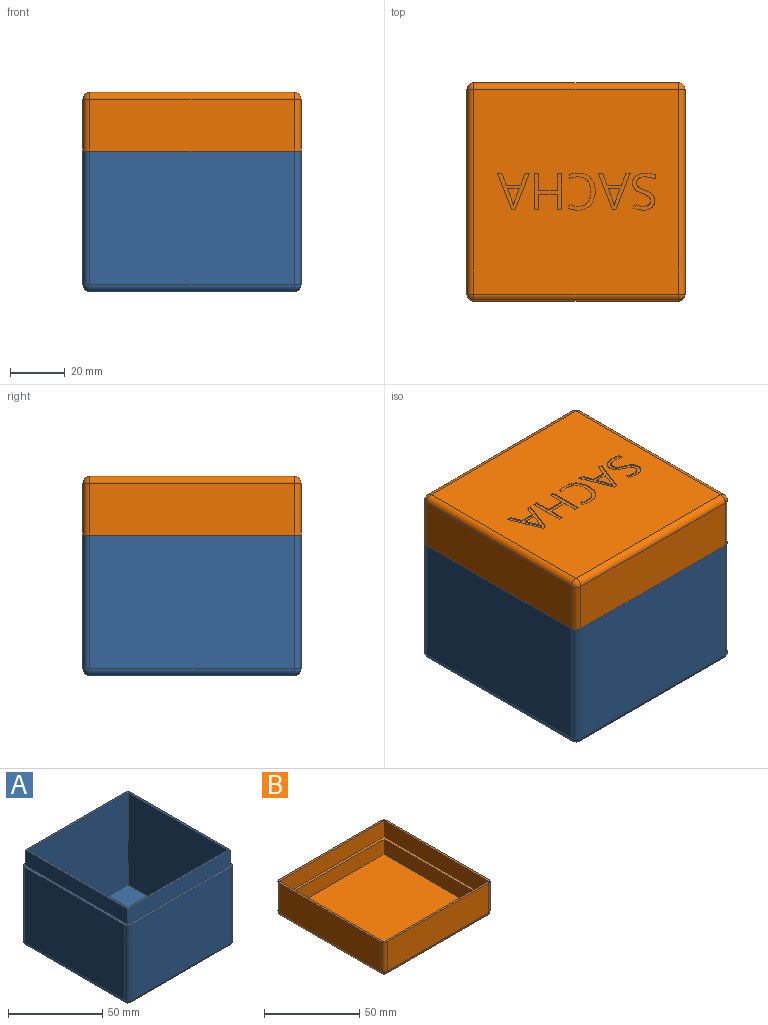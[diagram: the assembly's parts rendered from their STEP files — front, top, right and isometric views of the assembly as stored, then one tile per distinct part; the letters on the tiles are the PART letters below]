
ASSEMBLY  parts=2 mates=1
PART A: 28 faces, bbox 80x80x61.5 mm
  f0: plane 80x80mm, normal (0,0,1), area 496.4mm2, adj f1,f2,f3,f4,f6,f8,f11,f17
  f1: plane 75x49mm, normal (1,0,0), area 3675mm2, adj f0,f11,f15,f17
  f2: plane 75x49mm, normal (0,1,0), area 3675mm2, adj f0,f8,f14,f17
  f3: plane 75x49mm, normal (-1,0,0), area 3675mm2, adj f0,f6,f8,f9
  f4: plane 75x49mm, normal (0,-1,0), area 3675mm2, adj f0,f6,f10,f11
  f5: plane 75x75mm, normal (0,0,-1), area 5625mm2, adj f9,f10,f14,f15
  f6: cylinder r=2.5mm len=49mm, axis (0,0,1), area 192.4mm2, adj f0,f3,f4,f7
  f7: sphere r=2.5mm, area 9.8mm2, adj f6,f9,f10
  f8: cylinder r=2.5mm len=49mm, axis (0,0,-1), area 192.4mm2, adj f0,f2,f3,f12
  f9: cylinder r=2.5mm len=75mm, axis (0,-1,0), area 294.5mm2, adj f3,f5,f7,f12
  f10: cylinder r=2.5mm len=75mm, axis (1,0,0), area 294.5mm2, adj f4,f5,f7,f13
  f11: cylinder r=2.5mm len=49mm, axis (0,0,-1), area 192.4mm2, adj f0,f1,f4,f13
  f12: sphere r=2.5mm, area 9.8mm2, adj f8,f9,f14
  f13: sphere r=2.5mm, area 9.8mm2, adj f10,f11,f15
  f14: cylinder r=2.5mm len=75mm, axis (-1,0,0), area 294.5mm2, adj f2,f5,f12,f16
  f15: cylinder r=2.5mm len=75mm, axis (0,1,0), area 294.5mm2, adj f1,f5,f13,f16
  f16: sphere r=2.5mm, area 9.8mm2, adj f14,f15,f17
  f17: cylinder r=2.5mm len=49mm, axis (0,0,1), area 192.4mm2, adj f0,f1,f2,f16
  f18: plane 76.8x10mm, normal (0,-1,0), area 768mm2, adj f0,f19,f21,f22
  f19: plane 76.8x10mm, normal (1,0,0), area 768mm2, adj f0,f18,f20,f22
  f20: plane 76.8x10mm, normal (0,1,0), area 768mm2, adj f0,f19,f21,f22
  f21: plane 76.8x10mm, normal (-1,0,0), area 768mm2, adj f0,f18,f20,f22
  f22: plane 76.8x76.8mm, normal (0,0,1), area 362.9mm2, adj f18,f19,f20,f21,f24,f25,f26,f27
  f23: plane 74.4x74.4mm, normal (0,0,1), area 5535.4mm2, adj f24,f25,f26,f27
  f24: plane 74.4x60mm, normal (0,-1,0), area 4464mm2, adj f22,f23,f25,f27
  f25: plane 74.4x60mm, normal (1,0,0), area 4464mm2, adj f22,f23,f24,f26
  f26: plane 74.4x60mm, normal (0,1,0), area 4464mm2, adj f22,f23,f25,f27
  f27: plane 74.4x60mm, normal (-1,0,0), area 4464mm2, adj f22,f23,f24,f26
PART B: 113 faces, bbox 80x80x21.5 mm
  f0: plane 75x75mm, normal (0,0,-1), area 5382.9mm2, adj f19,f20,f24,f25,f28,f29,f30,f31
  f1: plane 75x19mm, normal (1,0,0), area 1425mm2, adj f5,f21,f25,f27
  f2: plane 75x19mm, normal (0,1,0), area 1425mm2, adj f5,f18,f24,f27
  f3: plane 75x19mm, normal (-1,0,0), area 1425mm2, adj f5,f16,f18,f19
  f4: plane 75x19mm, normal (0,-1,0), area 1425mm2, adj f5,f16,f20,f21
  f5: plane 80x80mm, normal (0,0,1), area 372.9mm2, adj f1,f2,f3,f4,f6,f7,f8,f9
  f6: plane 77.6x10.4mm, normal (0,-1,0), area 807mm2, adj f5,f7,f9,f10
  f7: plane 77.6x10.4mm, normal (1,0,0), area 807mm2, adj f5,f6,f8,f10
  f8: plane 77.6x10.4mm, normal (0,1,0), area 807mm2, adj f5,f7,f9,f10
  f9: plane 77.6x10.4mm, normal (-1,0,0), area 807mm2, adj f5,f6,f8,f10
  f10: plane 77.6x77.6mm, normal (0,0,1), area 486.4mm2, adj f6,f7,f8,f9,f12,f13,f14,f15
  f11: plane 74.4x74.4mm, normal (0,0,1), area 5535.4mm2, adj f12,f13,f14,f15
  f12: plane 74.4x9.6mm, normal (0,1,0), area 714.2mm2, adj f10,f11,f13,f15
  f13: plane 74.4x9.6mm, normal (-1,0,0), area 714.2mm2, adj f10,f11,f12,f14
  f14: plane 74.4x9.6mm, normal (0,-1,0), area 714.2mm2, adj f10,f11,f13,f15
  f15: plane 74.4x9.6mm, normal (1,0,0), area 714.2mm2, adj f10,f11,f12,f14
  f16: cylinder r=2.5mm len=19mm, axis (0,0,1), area 74.6mm2, adj f3,f4,f5,f17
  f17: sphere r=2.5mm, area 9.8mm2, adj f16,f19,f20
  f18: cylinder r=2.5mm len=19mm, axis (0,0,-1), area 74.6mm2, adj f2,f3,f5,f22
  f19: cylinder r=2.5mm len=75mm, axis (0,-1,0), area 294.5mm2, adj f0,f3,f17,f22
  f20: cylinder r=2.5mm len=75mm, axis (1,0,0), area 294.5mm2, adj f0,f4,f17,f23
  f21: cylinder r=2.5mm len=19mm, axis (0,0,-1), area 74.6mm2, adj f1,f4,f5,f23
  f22: sphere r=2.5mm, area 9.8mm2, adj f18,f19,f24
  f23: sphere r=2.5mm, area 9.8mm2, adj f20,f21,f25
  f24: cylinder r=2.5mm len=75mm, axis (-1,0,0), area 294.5mm2, adj f0,f2,f22,f26
  f25: cylinder r=2.5mm len=75mm, axis (0,1,0), area 294.5mm2, adj f0,f1,f23,f26
  f26: sphere r=2.5mm, area 9.8mm2, adj f24,f25,f27
  f27: cylinder r=2.5mm len=19mm, axis (0,0,1), area 74.6mm2, adj f1,f2,f5,f26
  f28: extruded ~3.43x1.45mm, area 1.5mm2, adj f0,f29,f42,f43
  f29: extruded ~3x0.7mm, area 1.2mm2, adj f0,f28,f30,f43
  f30: plane 1.32x0.65mm, normal (-0.9,-0.44,0), area 0.6mm2, adj f0,f29,f31,f43
  f31: extruded ~3.63x0.76mm, area 1.5mm2, adj f0,f30,f32,f43
  f32: extruded ~3.39x0.83mm, area 1.4mm2, adj f0,f31,f33,f43
  f33: extruded ~2.36x2.2mm, area 1.3mm2, adj f0,f32,f34,f43
  f34: extruded ~3.57x0.76mm, area 1.5mm2, adj f0,f33,f35,f43
  f35: extruded ~5.03x1.58mm, area 2.2mm2, adj f0,f34,f36,f43
  f36: extruded ~4.5x1.77mm, area 2mm2, adj f0,f35,f37,f43
  f37: extruded ~3.38x0.52mm, area 1.4mm2, adj f0,f36,f38,f43
  f38: plane 1.34x0.4mm, normal (-1,0,0), area 0.5mm2, adj f0,f37,f39,f43
  f39: extruded ~3.15x0.5mm, area 1.3mm2, adj f0,f38,f40,f43
  f40: extruded ~3.46x1.41mm, area 1.5mm2, adj f0,f39,f41,f43
  f41: extruded ~4x1.21mm, area 1.7mm2, adj f0,f40,f42,f43
  f42: extruded ~3.96x1.26mm, area 1.7mm2, adj f0,f28,f41,f43
  f43: plane 13.56x9.98mm, normal (0,0,-1), area 38mm2, adj f28,f29,f30,f31,f32,f33,f34,f35
  f44: plane 1.53x0.4mm, normal (0,-1,0), area 0.6mm2, adj f0,f45,f55,f56
  f45: plane 13.19x0.4mm, normal (-1,0,0), area 5.3mm2, adj f0,f44,f46,f56
  f46: plane 1.53x0.4mm, normal (0,1,0), area 0.6mm2, adj f0,f45,f47,f56
  f47: plane 5.61x0.4mm, normal (1,0,0), area 2.2mm2, adj f0,f46,f48,f56
  f48: plane 6.95x0.4mm, normal (0,1,0), area 2.8mm2, adj f0,f47,f49,f56
  f49: plane 5.61x0.4mm, normal (-1,0,0), area 2.2mm2, adj f0,f48,f50,f56
  f50: plane 1.53x0.4mm, normal (0,1,0), area 0.6mm2, adj f0,f49,f51,f56
  f51: plane 13.19x0.4mm, normal (1,0,0), area 5.3mm2, adj f0,f50,f52,f56
  f52: plane 1.53x0.4mm, normal (0,-1,0), area 0.6mm2, adj f0,f51,f53,f56
  f53: plane 6.21x0.4mm, normal (-1,0,0), area 2.5mm2, adj f0,f52,f54,f56
  f54: plane 6.95x0.4mm, normal (0,-1,0), area 2.8mm2, adj f0,f53,f55,f56
  f55: plane 6.21x0.4mm, normal (1,0,0), area 2.5mm2, adj f0,f44,f54,f56
  f56: plane 13.19x10.01mm, normal (0,0,-1), area 49.9mm2, adj f44,f45,f46,f47,f48,f49,f50,f51
  f57: plane 4.09x1.54mm, normal (0.94,-0.35,0), area 1.7mm2, adj f58,f69,f70,f111
  f58: plane 4.27x0.4mm, normal (0,1,0), area 1.7mm2, adj f57,f59,f70,f111
  f59: plane 4.09x1.55mm, normal (-0.94,-0.35,0), area 1.7mm2, adj f58,f60,f70,f111
  f60: extruded ~1.9x0.57mm, area 0.8mm2, adj f59,f69,f70,f111
  f61: plane 4.19x1.64mm, normal (0.93,-0.36,0), area 1.8mm2, adj f0,f62,f68,f70
  f62: plane 1.59x0.4mm, normal (0,-1,0), area 0.6mm2, adj f0,f61,f63,f70
  f63: plane 13.24x5.19mm, normal (-0.93,0.36,0), area 5.7mm2, adj f0,f62,f64,f70
  f64: plane 1.29x0.4mm, normal (0,1,0), area 0.5mm2, adj f0,f63,f65,f70
  f65: plane 13.24x5.21mm, normal (0.93,0.37,0), area 5.7mm2, adj f0,f64,f66,f70
  f66: plane 1.55x0.4mm, normal (0,-1,0), area 0.6mm2, adj f0,f65,f67,f70
  f67: plane 4.19x1.62mm, normal (-0.93,-0.36,0), area 1.8mm2, adj f0,f66,f68,f70
  f68: plane 5.28x0.4mm, normal (0,-1,0), area 2.1mm2, adj f0,f61,f67,f70
  f69: extruded ~1.9x0.61mm, area 0.8mm2, adj f57,f60,f70,f111
  f70: plane 13.24x11.69mm, normal (0,0,-1), area 44.7mm2, adj f57,f58,f59,f60,f61,f62,f63,f64
  f71: plane 4.09x1.54mm, normal (0.94,-0.35,0), area 1.7mm2, adj f72,f83,f84,f112
  f72: plane 4.27x0.4mm, normal (0,1,0), area 1.7mm2, adj f71,f73,f84,f112
  f73: plane 4.09x1.55mm, normal (-0.94,-0.35,0), area 1.7mm2, adj f72,f74,f84,f112
  f74: extruded ~1.9x0.57mm, area 0.8mm2, adj f73,f83,f84,f112
  f75: plane 4.19x1.64mm, normal (0.93,-0.36,0), area 1.8mm2, adj f0,f76,f82,f84
  f76: plane 1.59x0.4mm, normal (0,-1,0), area 0.6mm2, adj f0,f75,f77,f84
  f77: plane 13.24x5.19mm, normal (-0.93,0.36,0), area 5.7mm2, adj f0,f76,f78,f84
  f78: plane 1.29x0.4mm, normal (0,1,0), area 0.5mm2, adj f0,f77,f79,f84
  f79: plane 13.24x5.21mm, normal (0.93,0.37,0), area 5.7mm2, adj f0,f78,f80,f84
  f80: plane 1.55x0.4mm, normal (0,-1,0), area 0.6mm2, adj f0,f79,f81,f84
  f81: plane 4.19x1.62mm, normal (-0.93,-0.36,0), area 1.8mm2, adj f0,f80,f82,f84
  f82: plane 5.28x0.4mm, normal (0,-1,0), area 2.1mm2, adj f0,f75,f81,f84
  f83: extruded ~1.9x0.61mm, area 0.8mm2, adj f71,f74,f84,f112
  f84: plane 13.24x11.69mm, normal (0,0,-1), area 44.7mm2, adj f71,f72,f73,f74,f75,f76,f77,f78
  f85: extruded ~2.72x1.26mm, area 1.2mm2, adj f0,f86,f109,f110
  f86: extruded ~2.2x0.78mm, area 1mm2, adj f0,f85,f87,f110
  f87: extruded ~2.85x1.59mm, area 1.3mm2, adj f0,f86,f88,f110
  f88: extruded ~1.84x0.81mm, area 0.8mm2, adj f0,f87,f89,f110
  f89: extruded ~0.85x0.8mm, area 0.5mm2, adj f0,f88,f90,f110
  f90: extruded ~1.12x0.4mm, area 0.5mm2, adj f0,f89,f91,f110
  f91: extruded ~1.45x0.69mm, area 0.7mm2, adj f0,f90,f92,f110
  f92: extruded ~1.9x0.52mm, area 0.8mm2, adj f0,f91,f93,f110
  f93: extruded ~3.18x0.68mm, area 1.3mm2, adj f0,f92,f94,f110
  f94: plane 1.33x0.48mm, normal (-0.94,-0.34,0), area 0.6mm2, adj f0,f93,f95,f110
  f95: extruded ~3.62x0.72mm, area 1.5mm2, adj f0,f94,f96,f110
  f96: extruded ~3.03x0.9mm, area 1.3mm2, adj f0,f95,f97,f110
  f97: extruded ~2.43x1.14mm, area 1.1mm2, adj f0,f96,f98,f110
  f98: extruded ~2.35x0.79mm, area 1mm2, adj f0,f97,f99,f110
  f99: extruded ~2.63x1.56mm, area 1.2mm2, adj f0,f98,f100,f110
  f100: extruded ~1.96x0.84mm, area 0.9mm2, adj f0,f99,f101,f110
  f101: extruded ~0.92x0.81mm, area 0.5mm2, adj f0,f100,f102,f110
  f102: extruded ~1.12x0.4mm, area 0.5mm2, adj f0,f101,f103,f110
  f103: extruded ~1.62x0.78mm, area 0.7mm2, adj f0,f102,f104,f110
  f104: extruded ~2.31x0.58mm, area 1mm2, adj f0,f103,f105,f110
  f105: extruded ~1.89x0.4mm, area 0.8mm2, adj f0,f104,f106,f110
  f106: extruded ~1.77x0.54mm, area 0.7mm2, adj f0,f105,f107,f110
  f107: plane 1.48x0.4mm, normal (1,0,0), area 0.6mm2, adj f0,f106,f108,f110
  f108: extruded ~3.61x0.61mm, area 1.5mm2, adj f0,f107,f109,f110
  f109: extruded ~3.43x0.98mm, area 1.5mm2, adj f0,f85,f108,f110
  f110: plane 13.56x8.3mm, normal (0,0,-1), area 40.3mm2, adj f85,f86,f87,f88,f89,f90,f91,f92
  f111: plane 5.99x4.27mm, normal (0,0,-1), area 12.2mm2, adj f57,f58,f59,f60,f69
  f112: plane 5.99x4.27mm, normal (0,0,-1), area 12.2mm2, adj f71,f72,f73,f74,f83
PLACE A t=(-21.85,-4.63,-18.77)mm fixed
PLACE B rot(axis=(0,1,0),180deg) t=(-21.85,-4.63,54.29)mm
MATE slider B.f11 <-> A.f23  axis (0,0,-1) through (-21.85,-4.63,52.79)mm
